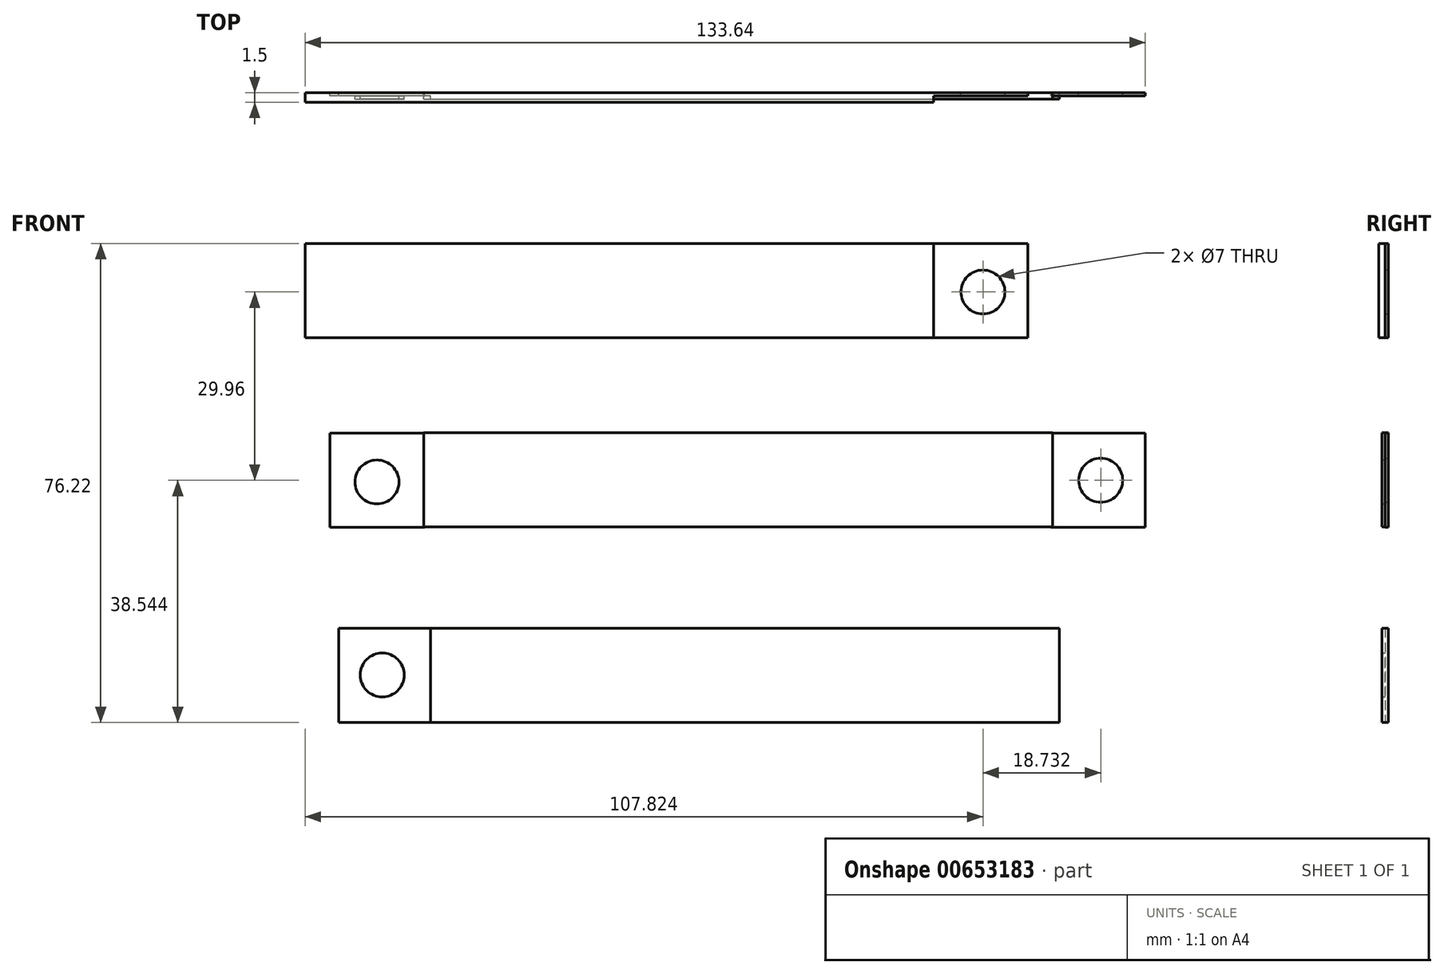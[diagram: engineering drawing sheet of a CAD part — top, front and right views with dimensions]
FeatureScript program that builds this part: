
annotation { "Feature Type Name" : "Feature", "Feature Type Description" : "" }
export const myFeature = defineFeature(function(context is Context, id is Id, definition is map)
    precondition{}
    {
        {
            var Q0;
            Q0=qCreatedBy(makeId("Front.planeOp"),FACE);
            var sketch = newSketch(context, id + "F0", { "sketchPlane" : qUnion([Q0])});
            skLineSegment(sketch, "E0.bottom", {"start": v(-69.83, 54.03) * mm, "end": v(30.17, 54.03) * mm});
            skLineSegment(sketch, "E0.top", {"start": v(-69.83, 39.03) * mm, "end": v(30.17, 39.03) * mm});
            skLineSegment(sketch, "E0.left", {"start": v(-69.83, 54.03) * mm, "end": v(-69.83, 39.03) * mm});
            skLineSegment(sketch, "E0.right", {"start": v(30.17, 54.03) * mm, "end": v(30.17, 39.03) * mm});
            skSolve(sketch);
        }
        {
            var Q0;
            Q0 = qSketchRegion(id + "F0", true);
            extrude(context, id + "F1", {"entities" : qUnion([Q0]), "depth" : 1.5 * mm, "offsetDistance" : 25.4 * mm});
        }
        {
            var Q0;
            Q0=qCreatedBy(makeId("Front.planeOp"),FACE);
            var sketch = newSketch(context, id + "F2", { "sketchPlane" : qUnion([Q0])});
            skLineSegment(sketch, "E1.bottom", {"start": v(-50.91, 23.9) * mm, "end": v(49.09, 23.9) * mm});
            skLineSegment(sketch, "E1.top", {"start": v(-50.91, 8.9) * mm, "end": v(49.09, 8.9) * mm});
            skLineSegment(sketch, "E1.left", {"start": v(-50.91, 23.9) * mm, "end": v(-50.91, 8.9) * mm});
            skLineSegment(sketch, "E1.right", {"start": v(49.09, 23.9) * mm, "end": v(49.09, 8.9) * mm});
            skSolve(sketch);
        }
        {
            var Q0;
            Q0 = qSketchRegion(id + "F2", true);
            extrude(context, id + "F3", {"entities" : qUnion([Q0]), "depth" : 1 * mm, "offsetDistance" : 25.4 * mm});
        }
        {
            var Q0;
            Q0=qCreatedBy(makeId("Front.planeOp"),FACE);
            var sketch = newSketch(context, id + "F4", { "sketchPlane" : qUnion([Q0])});
            skLineSegment(sketch, "E2.bottom", {"start": v(-49.84, -7.18) * mm, "end": v(50.16, -7.18) * mm});
            skLineSegment(sketch, "E2.top", {"start": v(-49.84, -22.18) * mm, "end": v(50.16, -22.18) * mm});
            skLineSegment(sketch, "E2.left", {"start": v(-49.84, -7.18) * mm, "end": v(-49.84, -22.18) * mm});
            skLineSegment(sketch, "E2.right", {"start": v(50.16, -7.18) * mm, "end": v(50.16, -22.18) * mm});
            skSolve(sketch);
        }
        {
            var Q0;
            Q0 = qSketchRegion(id + "F4", true);
            extrude(context, id + "F5", {"entities" : qUnion([Q0]), "depth" : 1 * mm, "offsetDistance" : 25.4 * mm});
        }
        {
            var Q0;
            Q0=qCreatedBy(makeId("Front.planeOp"),FACE);
            var sketch = newSketch(context, id + "F6", { "sketchPlane" : qUnion([Q0])});
            skLineSegment(sketch, "E3.bottom", {"start": v(30.16, 54.03) * mm, "end": v(45.16, 54.03) * mm});
            skLineSegment(sketch, "E3.top", {"start": v(30.16, 39.03) * mm, "end": v(45.16, 39.03) * mm});
            skLineSegment(sketch, "E3.left", {"start": v(30.16, 54.03) * mm, "end": v(30.16, 39.03) * mm});
            skLineSegment(sketch, "E3.right", {"start": v(45.16, 54.03) * mm, "end": v(45.16, 39.03) * mm});
            skSolve(sketch);
        }
        {
            var Q0;
            Q0 = qSketchRegion(id + "F6", true);
            extrude(context, id + "F7", {"entities" : qUnion([Q0]), "operationType" : NewBodyOperationType.ADD, "depth" : 0.5 * mm, "offsetDistance" : 25.4 * mm});
        }
        {
            var Q0;
            Q0=qCreatedBy(makeId("Front.planeOp"),FACE);
            var sketch = newSketch(context, id + "F8", { "sketchPlane" : qUnion([Q0])});
            skLineSegment(sketch, "E4.bottom", {"start": v(48.81, 23.88) * mm, "end": v(63.81, 23.88) * mm});
            skLineSegment(sketch, "E4.top", {"start": v(48.81, 8.88) * mm, "end": v(63.81, 8.88) * mm});
            skLineSegment(sketch, "E4.left", {"start": v(48.81, 23.88) * mm, "end": v(48.81, 8.88) * mm});
            skLineSegment(sketch, "E4.right", {"start": v(63.81, 23.88) * mm, "end": v(63.81, 8.88) * mm});
            skSolve(sketch);
        }
        {
            var Q0;
            Q0 = qSketchRegion(id + "F8", true);
            extrude(context, id + "F9", {"entities" : qUnion([Q0]), "operationType" : NewBodyOperationType.ADD, "depth" : 0.5 * mm, "offsetDistance" : 25.4 * mm});
        }
        {
            var Q0;
            Q0=qCreatedBy(makeId("Front.planeOp"),FACE);
            var sketch = newSketch(context, id + "F10", { "sketchPlane" : qUnion([Q0])});
            skCircle(sketch, "E5", {"center": v(38, 46.31) * mm, "radius": 3.5 * mm});
            skSolve(sketch);
        }
        {
            var Q0;
            Q0 = qSketchRegion(id + "F10", true);
            extrude(context, id + "F11", {"entities" : qUnion([Q0]), "operationType" : NewBodyOperationType.REMOVE, "depth" : 25.4 * mm, "offsetDistance" : 25.4 * mm});
        }
        {
            var Q0;
            Q0=qCreatedBy(makeId("Front.planeOp"),FACE);
            var sketch = newSketch(context, id + "F12", { "sketchPlane" : qUnion([Q0])});
            skCircle(sketch, "E6", {"center": v(56.73, 16.35) * mm, "radius": 3.5 * mm});
            skSolve(sketch);
        }
        {
            var Q0;
            Q0 = qSketchRegion(id + "F12", true);
            extrude(context, id + "F13", {"entities" : qUnion([Q0]), "operationType" : NewBodyOperationType.REMOVE, "depth" : 25.4 * mm, "offsetDistance" : 25.4 * mm});
        }
        {
            var Q0;
            Q0=qCreatedBy(makeId("Front.planeOp"),FACE);
            var sketch = newSketch(context, id + "F14", { "sketchPlane" : qUnion([Q0])});
            skLineSegment(sketch, "E7.bottom", {"start": v(-50.84, 23.89) * mm, "end": v(-65.84, 23.89) * mm});
            skLineSegment(sketch, "E7.top", {"start": v(-50.84, 8.89) * mm, "end": v(-65.84, 8.89) * mm});
            skLineSegment(sketch, "E7.left", {"start": v(-50.84, 23.89) * mm, "end": v(-50.84, 8.89) * mm});
            skLineSegment(sketch, "E7.right", {"start": v(-65.84, 23.89) * mm, "end": v(-65.84, 8.89) * mm});
            skSolve(sketch);
        }
        {
            var Q0;
            Q0 = qSketchRegion(id + "F14", true);
            extrude(context, id + "F15", {"entities" : qUnion([Q0]), "operationType" : NewBodyOperationType.ADD, "depth" : 0.5 * mm, "offsetDistance" : 25.4 * mm});
        }
        {
            var Q0;
            Q0=qCreatedBy(makeId("Front.planeOp"),FACE);
            var sketch = newSketch(context, id + "F16", { "sketchPlane" : qUnion([Q0])});
            skCircle(sketch, "E8", {"center": v(-58.38, 16.09) * mm, "radius": 3.5 * mm});
            skSolve(sketch);
        }
        {
            var Q0;
            Q0 = qSketchRegion(id + "F16", true);
            extrude(context, id + "F17", {"entities" : qUnion([Q0]), "operationType" : NewBodyOperationType.ADD, "depth" : 1 * mm, "offsetDistance" : 25.4 * mm});
        }
        {
            var Q0;
            Q0=qCreatedBy(makeId("Front.planeOp"),FACE);
            var sketch = newSketch(context, id + "F18", { "sketchPlane" : qUnion([Q0])});
            skLineSegment(sketch, "E9.bottom", {"start": v(-49.47, -7.19) * mm, "end": v(-64.47, -7.19) * mm});
            skLineSegment(sketch, "E9.top", {"start": v(-49.47, -22.19) * mm, "end": v(-64.47, -22.19) * mm});
            skLineSegment(sketch, "E9.left", {"start": v(-49.47, -7.19) * mm, "end": v(-49.47, -22.19) * mm});
            skLineSegment(sketch, "E9.right", {"start": v(-64.47, -7.19) * mm, "end": v(-64.47, -22.19) * mm});
            skSolve(sketch);
        }
        {
            var Q0;
            Q0 = qSketchRegion(id + "F18", true);
            extrude(context, id + "F19", {"entities" : qUnion([Q0]), "operationType" : NewBodyOperationType.ADD, "depth" : 0.5 * mm, "offsetDistance" : 25.4 * mm});
        }
        {
            var Q0;
            Q0=qCreatedBy(makeId("Front.planeOp"),FACE);
            var sketch = newSketch(context, id + "F20", { "sketchPlane" : qUnion([Q0])});
            skCircle(sketch, "E10", {"center": v(-57.55, -14.63) * mm, "radius": 3.5 * mm});
            skSolve(sketch);
        }
        {
            var Q0;
            Q0 = qSketchRegion(id + "F20", true);
            extrude(context, id + "F21", {"entities" : qUnion([Q0]), "operationType" : NewBodyOperationType.ADD, "depth" : 1 * mm, "offsetDistance" : 25.4 * mm});
        }
    });
